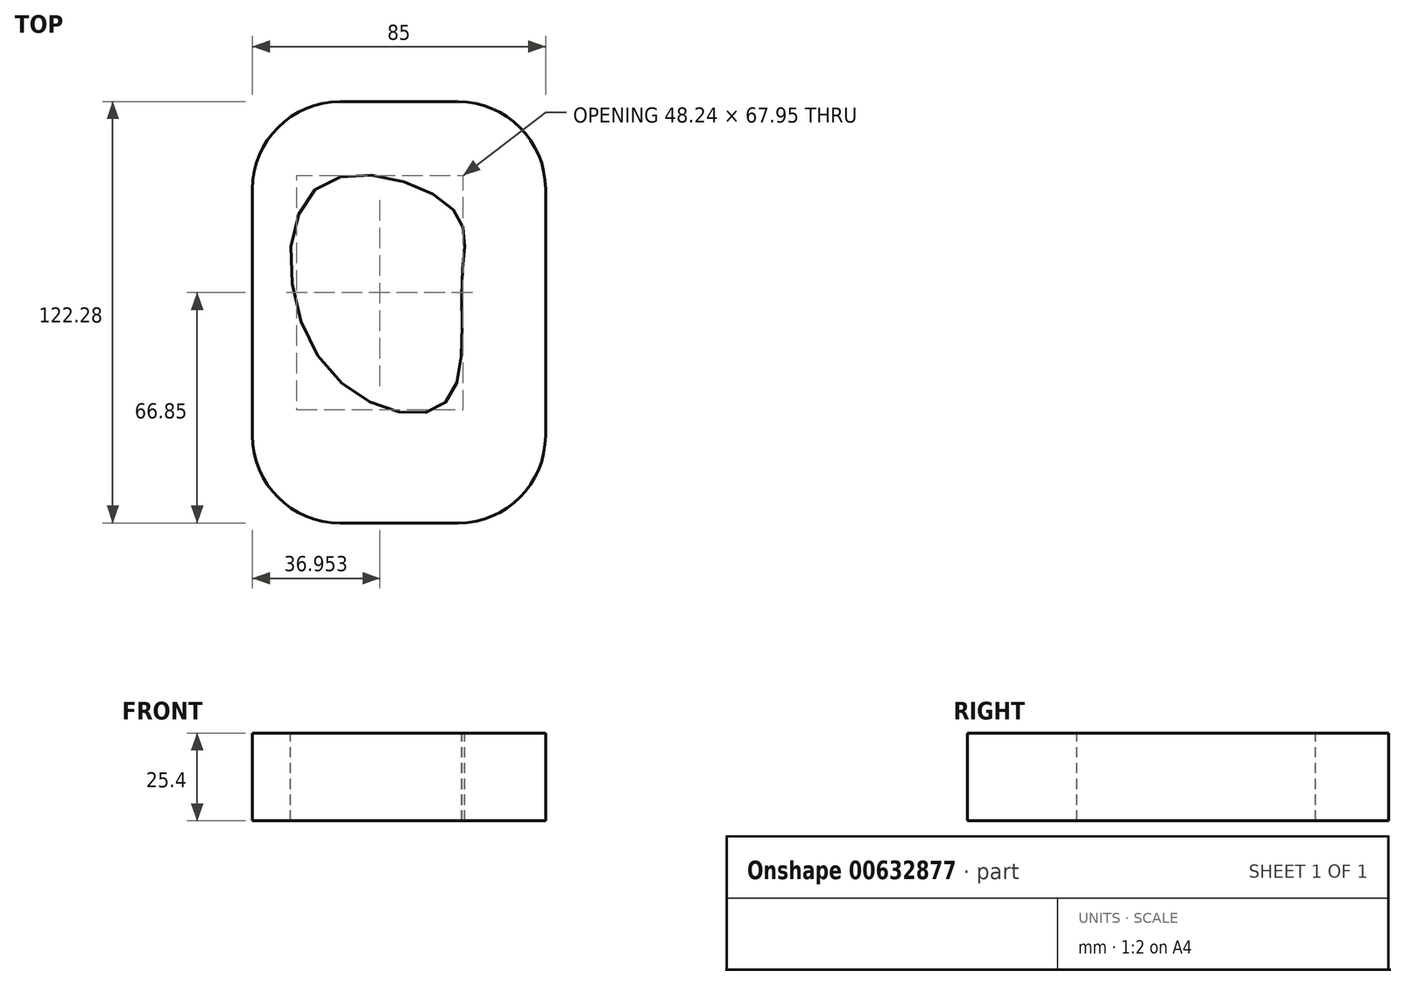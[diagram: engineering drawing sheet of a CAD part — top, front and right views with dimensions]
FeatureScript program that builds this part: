
annotation { "Feature Type Name" : "Feature", "Feature Type Description" : "" }
export const myFeature = defineFeature(function(context is Context, id is Id, definition is map)
    precondition{}
    {
        {
            var Q0;
            Q0=qCreatedBy(makeId("Top.planeOp"),FACE);
            var sketch = newSketch(context, id + "F0", { "sketchPlane" : qUnion([Q0])});
            skLineSegment(sketch, "E0.bottom", {"start": v(42.5, 61.14) * mm, "end": v(-42.5, 61.14) * mm});
            skLineSegment(sketch, "E0.top", {"start": v(42.5, -61.14) * mm, "end": v(-42.5, -61.14) * mm});
            skLineSegment(sketch, "E0.left", {"start": v(42.5, 61.14) * mm, "end": v(42.5, -61.14) * mm});
            skLineSegment(sketch, "E0.right", {"start": v(-42.5, 61.14) * mm, "end": v(-42.5, -61.14) * mm});
            skPoint(sketch, "E0.middle", {"position": v(0, 0) * mm});
            skSolve(sketch);
        }
        {
            var Q0;
            Q0 = qSketchRegion(id + "F0", true);
            extrude(context, id + "F1", {"entities" : qUnion([Q0]), "endBound" : BoundingType.SYMMETRIC, "depth" : 25.4 * mm, "offsetDistance" : 25.4 * mm});
        }
        {
            var Q0;
            Q0=makeQuery(id+"F1.opExtrude","CAP_FACE",FACE,{"disambiguationData":[OSD([sQuery(id+"F0.wireOp",EDGE,"E0.bottom"),sQuery(id+"F0.wireOp",EDGE,"E0.top"),sQuery(id+"F0.wireOp",EDGE,"E0.left"),sQuery(id+"F0.wireOp",EDGE,"E0.right")])],"isStart":false});
            var sketch = newSketch(context, id + "F2", { "sketchPlane" : qUnion([Q0])});
            skFitSpline(sketch, "E1", {"points": [v(15.8, 29.75) * mm, v(-23.02, 36.6) * mm, v(-21.72, -15.16) * mm, v(13.21, -26.44) * mm, v(18.2, 8.68) * mm, v(15.8, 29.75) * mm]});
            skSolve(sketch);
        }
        {
            var Q0;
            Q0 = qSketchRegion(id + "F2", true);
            extrude(context, id + "F3", {"entities" : qUnion([Q0]), "operationType" : NewBodyOperationType.REMOVE, "oppositeDirection" : true, "depth" : 25.4 * mm, "offsetDistance" : 25.4 * mm});
        }
        {
            var Q0;
            Q0=makeQuery(id+"F1.opExtrude","SWEPT_EDGE",EDGE,{"disambiguationData":[OSD([sQuery(id+"F0.wireOp",EDGE,"E0.top"),sQuery(id+"F0.wireOp",EDGE,"E0.right")])]});
            var Q1;
            Q1=makeQuery(id+"F1.opExtrude","SWEPT_EDGE",EDGE,{"disambiguationData":[OSD([sQuery(id+"F0.wireOp",EDGE,"E0.top"),sQuery(id+"F0.wireOp",EDGE,"E0.left")])]});
            var Q2;
            Q2=makeQuery(id+"F1.opExtrude","SWEPT_EDGE",EDGE,{"disambiguationData":[OSD([sQuery(id+"F0.wireOp",EDGE,"E0.bottom"),sQuery(id+"F0.wireOp",EDGE,"E0.left")])]});
            var Q3;
            Q3=makeQuery(id+"F1.opExtrude","SWEPT_EDGE",EDGE,{"disambiguationData":[OSD([sQuery(id+"F0.wireOp",EDGE,"E0.bottom"),sQuery(id+"F0.wireOp",EDGE,"E0.right")])]});
            fillet(context, id + "F4", {"entities" : qUnion([Q0, Q1, Q2, Q3]), "radius" : 25.4 * mm, "tangentPropagation" : true, "allowEdgeOverflow" : false});
        }
    });
